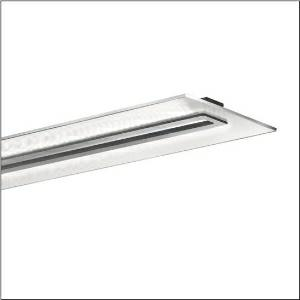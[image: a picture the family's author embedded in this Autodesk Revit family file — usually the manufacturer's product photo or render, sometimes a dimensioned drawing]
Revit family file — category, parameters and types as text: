
# Revit family: vega_r__11_5mn238dle003_bbe2
name_source: partatom
category: Lighting Fixtures
units: mm (PartAtom-declared; Revit-internal decimal feet)

## family parameters
Cut with Voids When Loaded = No
Host = Face
Light Source = No
Part Type = Normal
Room Calculation Point = No
Round Connector Dimension = Use Diameter
Shared = No

## types (1)
- --- (1 x LED 3000K / CRI = 80 (unbekannt), 7300 lm, 3000K)
    Apparent Load = 62 VA
    CIE Flux Codes = 61 86 97 62 100
    Color Rendering = 80
    Color Temperature = 3000K
    Default Elevation = 1800 mm
    Description = Vega® 11, office luminaire, primary light control with prismatic reflector, of PMMA, transparent prismatic structure, CAT 2 (L<= 1500cd/m²), light emission: direct/indirect distribution, primary light characteristic: symmetric, installation type: suspended mounting, surface-mounted, LED, rated luminous flux: 7.300lm, luminous efficacy: 118lm/W, light colour: 830, colour temperature: 3000K, control gear: DALI, with terminal, 3+2-pole, max. 2.5mm², mains connection: 230V, AC, 50Hz, connection cable inclusive, cable length: 1,5m, rated input power: 62W, luminaire housing, rectangular, rounded, of aluminium section, anodised, metallic grey (RAL 9006), length: 1.250mm, width: 350mm, height: 43mm, luminaire housing, lower part, of aluminium section, anodised, metallic grey (RAL 9006), of PC, grey, protection rating (complete): IP20, insulation class (complete): insulation class I (protective earthing), certification: CE, standard: EN 50419, packaging unit: 1 piece
    Height = 40 mm  [stored 0.131234 ft]
    Lamp = 1 x LED 3000K / CRI >= 80 (unbekannt)
    Lamp Light Flux = 7300 lm
    Lamp count = 1
    Length = 1250 mm
    Luminous efficacy = 118 lm/W
    Manufacturer = Siteco
    ModVariant = No
    Model = 5MN238DLE003
    Mounting Place = Ceiling
    Mounting Type = Pendant
    Number of Poles = 1
    OnlyDefault = Yes
    Power Factor = 1
    Product Name = Vega® 11
    Product group = office luminaire | ceiling pendant
    ProductGroupID = 903
    Protection Class = Protection class I
    Protection Degree = IP 20
    RLX_Detail_Level = 1
    RLX_Emergency_Light_Flux = 0 lm
    RLX_Emergency_Type = 0
    RLX_Emergency_Type_DB = No
    RlxData = <blob elided: 62597 chars, md5=b7dd896a>
    Socket = socket
    Standby Power = 0 W
    System Light Flux = 7300 lm
    System Power = 62 W
    Type Comments = factory setting: luminous flux: 100 % | dim-lin: 254 | 460 mA
    Type Image = l_1004807.jpg
    URL = http://relux.com
    VarID = @adj_220841
    Voltage = 0 V
    Weight = 0.00 kg
    Width = 350 mm

note: [stored X ft] marks values corroborated as IEEE doubles in the binary element streams (Revit-internal decimal feet)

## geometry (parser evidence)
native form markers: Blend x4, Sweep x12
no freeform markers — native parametric forms only
